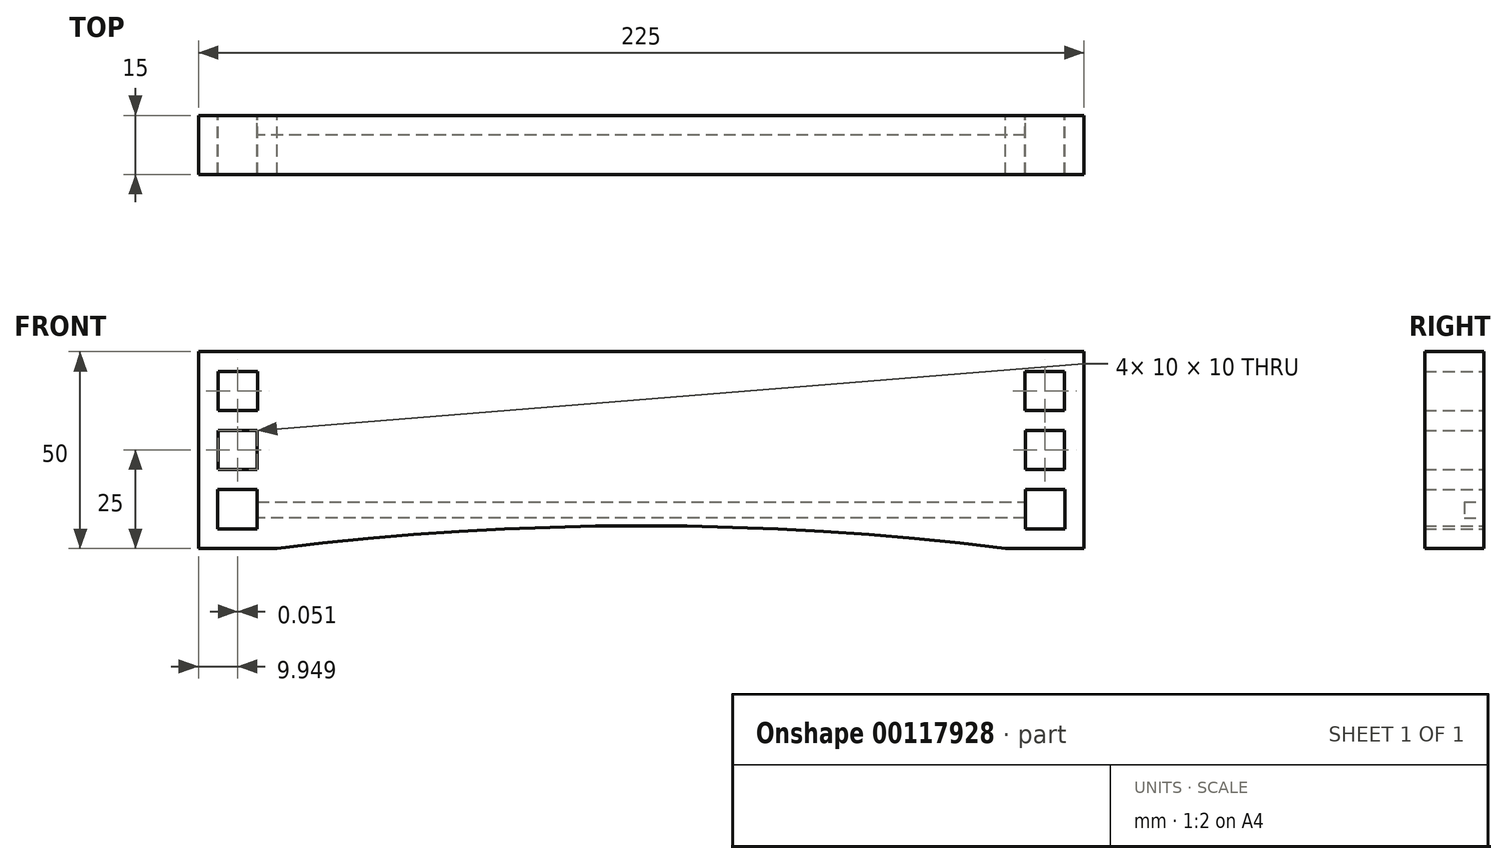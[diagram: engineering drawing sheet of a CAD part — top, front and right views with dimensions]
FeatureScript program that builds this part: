
annotation { "Feature Type Name" : "Feature", "Feature Type Description" : "" }
export const myFeature = defineFeature(function(context is Context, id is Id, definition is map)
    precondition{}
    {
        {
            var Q0;
            Q0=qCreatedBy(makeId("Front.planeOp"),FACE);
            var sketch = newSketch(context, id + "F0", { "sketchPlane" : qUnion([Q0])});
            skLineSegment(sketch, "E0.bottom", {"start": v(-112.5, -25) * mm, "end": v(-92.5, -25) * mm});
            skLineSegment(sketch, "E0.top", {"start": v(-112.5, 25) * mm, "end": v(112.5, 25) * mm});
            skLineSegment(sketch, "E0.left", {"start": v(-112.5, -25) * mm, "end": v(-112.5, 25) * mm});
            skLineSegment(sketch, "E0.right", {"start": v(112.5, -25) * mm, "end": v(112.5, 25) * mm});
            skLineSegment(sketch, "E1.trimOffspring", {"start": v(92.5, -25) * mm, "end": v(112.5, -25) * mm});
            skArc(sketch, "E2", {"start": v(92.5, -25) * mm, "mid": v(0, -19.27) * mm, "end": v(-92.5, -25) * mm});
            skPoint(sketch, "E3.orphan", {"position": v(-72.5, -25) * mm});
            skLineSegment(sketch, "E4.bottom", {"start": v(-107.5, 20) * mm, "end": v(-97.5, 20) * mm});
            skLineSegment(sketch, "E4.top", {"start": v(-107.5, 10) * mm, "end": v(-97.5, 10) * mm});
            skLineSegment(sketch, "E4.left", {"start": v(-107.5, 20) * mm, "end": v(-107.5, 10) * mm});
            skLineSegment(sketch, "E4.right", {"start": v(-97.5, 20) * mm, "end": v(-97.5, 10) * mm});
            skLineSegment(sketch, "E5.1.0.0", {"start": v(-107.55, 5) * mm, "end": v(-97.55, 5) * mm});
            skLineSegment(sketch, "E5.1.0.1", {"start": v(-107.55, -5) * mm, "end": v(-97.55, -4.97) * mm});
            skLineSegment(sketch, "E5.1.0.2", {"start": v(-107.55, 5) * mm, "end": v(-107.55, -5) * mm});
            skLineSegment(sketch, "E5.1.0.3", {"start": v(-97.55, 5) * mm, "end": v(-97.55, -4.97) * mm});
            skLineSegment(sketch, "E5.2.0.0", {"start": v(-107.6, -10) * mm, "end": v(-97.6, -9.97) * mm});
            skLineSegment(sketch, "E5.2.0.1", {"start": v(-107.6, -20) * mm, "end": v(-97.6, -20) * mm});
            skLineSegment(sketch, "E5.2.0.2", {"start": v(-107.6, -10) * mm, "end": v(-107.6, -20) * mm});
            skLineSegment(sketch, "E5.2.0.3", {"start": v(-97.6, -9.97) * mm, "end": v(-97.6, -20) * mm});
            skLineSegment(sketch, "E6.MirrorCS", {"start": v(107.5, 20) * mm, "end": v(107.5, 10) * mm});
            skLineSegment(sketch, "E7.MirrorCS", {"start": v(107.5, 10) * mm, "end": v(97.5, 10) * mm});
            skLineSegment(sketch, "E8.MirrorCS", {"start": v(107.5, 20) * mm, "end": v(97.5, 20) * mm});
            skLineSegment(sketch, "E9.MirrorCS", {"start": v(97.5, 20) * mm, "end": v(97.5, 10) * mm});
            skLineSegment(sketch, "E10.MirrorCS", {"start": v(107.55, 5) * mm, "end": v(107.55, -5) * mm});
            skLineSegment(sketch, "E11.MirrorCS", {"start": v(107.55, 5) * mm, "end": v(97.55, 5) * mm});
            skLineSegment(sketch, "E12.MirrorCS", {"start": v(97.55, 5) * mm, "end": v(97.55, -4.97) * mm});
            skLineSegment(sketch, "E13.MirrorCS", {"start": v(107.55, -5) * mm, "end": v(97.55, -4.97) * mm});
            skLineSegment(sketch, "E14.MirrorCS", {"start": v(107.6, -10) * mm, "end": v(107.6, -20) * mm});
            skLineSegment(sketch, "E15.MirrorCS", {"start": v(97.6, -9.97) * mm, "end": v(97.6, -20) * mm});
            skLineSegment(sketch, "E16.MirrorCS", {"start": v(107.6, -10) * mm, "end": v(97.6, -9.97) * mm});
            skLineSegment(sketch, "E17.MirrorCS", {"start": v(107.6, -20) * mm, "end": v(97.6, -20) * mm});
            skSolve(sketch);
        }
        {
            var Q0;
            Q0 = qSketchRegion(id + "F0", true);
            extrude(context, id + "F1", {"entities" : qUnion([Q0]), "depth" : 15 * mm});
        }
        {
            var Q0;
            Q0=makeQuery(id+"F1.opExtrude","CAP_FACE",FACE,{"disambiguationData":[OSD([sQuery(id+"F0.wireOp",EDGE,"E0.bottom"),sQuery(id+"F0.wireOp",EDGE,"E0.top"),sQuery(id+"F0.wireOp",EDGE,"E0.left"),sQuery(id+"F0.wireOp",EDGE,"E0.right"),sQuery(id+"F0.wireOp",EDGE,"E1.trimOffspring"),sQuery(id+"F0.wireOp",EDGE,"E2"),sQuery(id+"F0.wireOp",EDGE,"E4.bottom"),sQuery(id+"F0.wireOp",EDGE,"E4.top"),sQuery(id+"F0.wireOp",EDGE,"E4.left"),sQuery(id+"F0.wireOp",EDGE,"E4.right"),sQuery(id+"F0.wireOp",EDGE,"E5.1.0.0"),sQuery(id+"F0.wireOp",EDGE,"E5.1.0.1"),sQuery(id+"F0.wireOp",EDGE,"E5.1.0.2"),sQuery(id+"F0.wireOp",EDGE,"E5.1.0.3"),sQuery(id+"F0.wireOp",EDGE,"E5.2.0.0"),sQuery(id+"F0.wireOp",EDGE,"E5.2.0.1"),sQuery(id+"F0.wireOp",EDGE,"E5.2.0.2"),sQuery(id+"F0.wireOp",EDGE,"E5.2.0.3"),sQuery(id+"F0.wireOp",EDGE,"E6.MirrorCS"),sQuery(id+"F0.wireOp",EDGE,"E7.MirrorCS"),sQuery(id+"F0.wireOp",EDGE,"E8.MirrorCS"),sQuery(id+"F0.wireOp",EDGE,"E9.MirrorCS"),sQuery(id+"F0.wireOp",EDGE,"E10.MirrorCS"),sQuery(id+"F0.wireOp",EDGE,"E11.MirrorCS"),sQuery(id+"F0.wireOp",EDGE,"E12.MirrorCS"),sQuery(id+"F0.wireOp",EDGE,"E13.MirrorCS"),sQuery(id+"F0.wireOp",EDGE,"E14.MirrorCS"),sQuery(id+"F0.wireOp",EDGE,"E15.MirrorCS"),sQuery(id+"F0.wireOp",EDGE,"E16.MirrorCS"),sQuery(id+"F0.wireOp",EDGE,"E17.MirrorCS")])],"isStart":true});
            var sketch = newSketch(context, id + "F2", { "sketchPlane" : qUnion([Q0])});
            skLineSegment(sketch, "E18", {"start": v(-97.6, -17.23) * mm, "end": v(97.6, -17.23) * mm});
            skLineSegment(sketch, "E19", {"start": v(97.6, -17.23) * mm, "end": v(97.6, -13.23) * mm});
            skLineSegment(sketch, "E20", {"start": v(97.6, -13.23) * mm, "end": v(-97.6, -13.23) * mm});
            skLineSegment(sketch, "E21", {"start": v(-97.6, -13.23) * mm, "end": v(-97.6, -17.23) * mm});
            skSolve(sketch);
        }
        {
            var Q0;
            Q0 = qSketchRegion(id + "F2", true);
            extrude(context, id + "F3", {"entities" : qUnion([Q0]), "operationType" : NewBodyOperationType.REMOVE, "oppositeDirection" : true, "depth" : 5 * mm});
        }
    });
